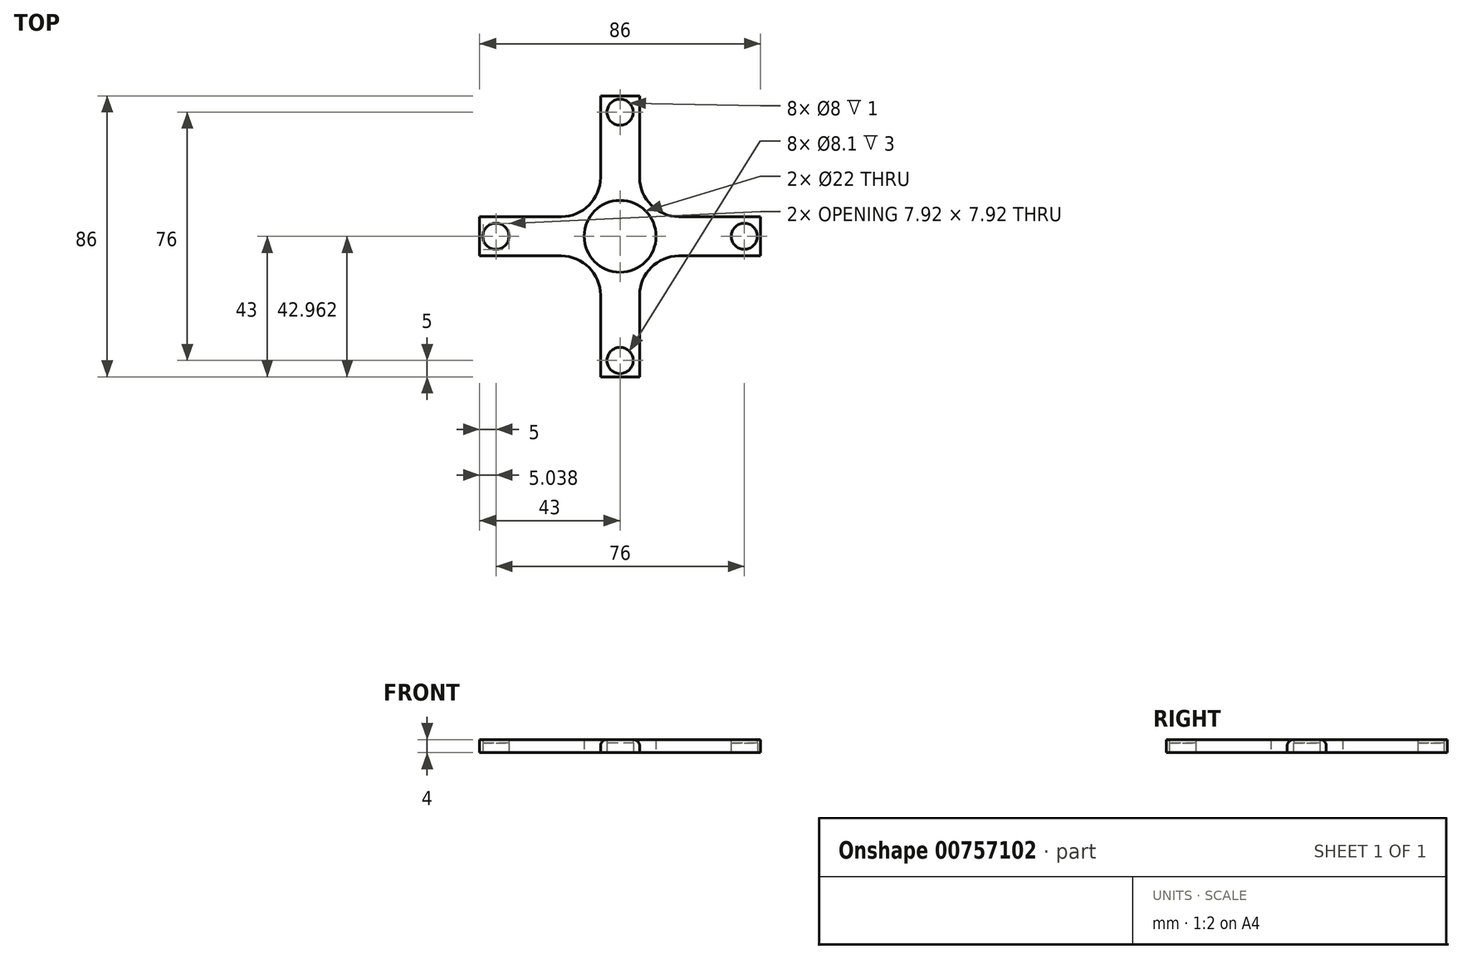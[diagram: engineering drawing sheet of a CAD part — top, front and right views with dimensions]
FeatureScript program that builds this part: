
annotation { "Feature Type Name" : "Feature", "Feature Type Description" : "" }
export const myFeature = defineFeature(function(context is Context, id is Id, definition is map)
    precondition{}
    {
        {
            var Q0;
            Q0=qCreatedBy(makeId("Top.planeOp"),FACE);
            var sketch = newSketch(context, id + "F0", { "sketchPlane" : qUnion([Q0])});
            skLineSegment(sketch, "E0.bottom", {"start": v(0, 0) * mm, "end": v(6, 0) * mm});
            skLineSegment(sketch, "E0.top", {"start": v(0, 38) * mm, "end": v(6, 38) * mm});
            skLineSegment(sketch, "E0.left", {"start": v(0, 0) * mm, "end": v(0, 38) * mm});
            skLineSegment(sketch, "E0.right", {"start": v(6, 18) * mm, "end": v(6, 38) * mm});
            skLineSegment(sketch, "E1.MirrorCS", {"start": v(0, 38) * mm, "end": v(-6, 38) * mm});
            skLineSegment(sketch, "E2.MirrorCS", {"start": v(-6, 18) * mm, "end": v(-6, 38) * mm});
            skLineSegment(sketch, "E3.MirrorCS", {"start": v(0, 0) * mm, "end": v(-6, 0) * mm});
            skLineSegment(sketch, "E4.1.0", {"start": v(-38, 0) * mm, "end": v(-38, -6) * mm});
            skLineSegment(sketch, "E4.1.1", {"start": v(-38, 0) * mm, "end": v(-38, 6) * mm});
            skLineSegment(sketch, "E4.1.2", {"start": v(-18, 6) * mm, "end": v(-38, 6) * mm});
            skLineSegment(sketch, "E4.1.3", {"start": v(-18, -6) * mm, "end": v(-38, -6) * mm});
            skLineSegment(sketch, "E4.1.4", {"start": v(0, 0) * mm, "end": v(0, -6) * mm});
            skLineSegment(sketch, "E4.1.5", {"start": v(0, 0) * mm, "end": v(0, 6) * mm});
            skLineSegment(sketch, "E4.2.0", {"start": v(0, -38) * mm, "end": v(6, -38) * mm});
            skLineSegment(sketch, "E4.2.1", {"start": v(0, -38) * mm, "end": v(-6, -38) * mm});
            skLineSegment(sketch, "E4.2.2", {"start": v(-6, -18) * mm, "end": v(-6, -38) * mm});
            skLineSegment(sketch, "E4.2.3", {"start": v(6, -18) * mm, "end": v(6, -38) * mm});
            skLineSegment(sketch, "E4.3.0", {"start": v(38, 0) * mm, "end": v(38, 6) * mm});
            skLineSegment(sketch, "E4.3.1", {"start": v(38, 0) * mm, "end": v(38, -6) * mm});
            skLineSegment(sketch, "E4.3.2", {"start": v(18, -6) * mm, "end": v(38, -6) * mm});
            skLineSegment(sketch, "E4.3.3", {"start": v(18, 6) * mm, "end": v(38, 6) * mm});
            skLineSegment(sketch, "E4.3.4", {"start": v(0, 0) * mm, "end": v(0, 6) * mm});
            skLineSegment(sketch, "E4.3.5", {"start": v(0, 0) * mm, "end": v(0, -6) * mm});
            skPoint(sketch, "E4.center", {"position": v(0, 0) * mm});
            skPoint(sketch, "E5.newPointA", {"position": v(-6, 0) * mm});
            skPoint(sketch, "E5.newPointB", {"position": v(0, 6) * mm});
            skArc(sketch, "E5.filletArc", {"start": v(-18, 6) * mm, "mid": v(-9.51, 9.51) * mm, "end": v(-6, 18) * mm});
            skPoint(sketch, "E6.newPointB", {"position": v(6, 0) * mm});
            skArc(sketch, "E6.filletArc", {"start": v(6, 18) * mm, "mid": v(9.51, 9.51) * mm, "end": v(18, 6) * mm});
            skPoint(sketch, "E7.newPointB", {"position": v(0, -6) * mm});
            skArc(sketch, "E7.filletArc", {"start": v(18, -6) * mm, "mid": v(9.51, -9.51) * mm, "end": v(6, -18) * mm});
            skArc(sketch, "E8.filletArc", {"start": v(-6, -18) * mm, "mid": v(-9.51, -9.51) * mm, "end": v(-18, -6) * mm});
            skCircle(sketch, "E9", {"center": v(38, 0) * mm, "radius": 4.05 * mm});
            skCircle(sketch, "E10", {"center": v(38, 0) * mm, "radius": 4 * mm});
            skLineSegment(sketch, "E11.bottom", {"start": v(38, 6) * mm, "end": v(43, 6) * mm});
            skLineSegment(sketch, "E11.top", {"start": v(38, -6) * mm, "end": v(43, -6) * mm});
            skLineSegment(sketch, "E11.left", {"start": v(38, 6) * mm, "end": v(38, -6) * mm});
            skLineSegment(sketch, "E11.right", {"start": v(43, 6) * mm, "end": v(43, -6) * mm});
            skLineSegment(sketch, "E12.1.0", {"start": v(-6, 38) * mm, "end": v(-6, 43) * mm});
            skLineSegment(sketch, "E12.1.1", {"start": v(-6, 43) * mm, "end": v(6, 43) * mm});
            skLineSegment(sketch, "E12.1.2", {"start": v(6, 38) * mm, "end": v(6, 43) * mm});
            skCircle(sketch, "E12.1.3", {"center": v(0, 38) * mm, "radius": 4 * mm});
            skCircle(sketch, "E12.1.4", {"center": v(0, 38) * mm, "radius": 4.05 * mm});
            skLineSegment(sketch, "E12.2.0", {"start": v(-38, -6) * mm, "end": v(-43, -6) * mm});
            skLineSegment(sketch, "E12.2.1", {"start": v(-43, -6) * mm, "end": v(-43, 6) * mm});
            skLineSegment(sketch, "E12.2.2", {"start": v(-38, 6) * mm, "end": v(-43, 6) * mm});
            skCircle(sketch, "E12.2.3", {"center": v(-38, 0) * mm, "radius": 4 * mm});
            skCircle(sketch, "E12.2.4", {"center": v(-38, 0) * mm, "radius": 4.05 * mm});
            skLineSegment(sketch, "E12.3.0", {"start": v(6, -38) * mm, "end": v(6, -43) * mm});
            skLineSegment(sketch, "E12.3.1", {"start": v(6, -43) * mm, "end": v(-6, -43) * mm});
            skLineSegment(sketch, "E12.3.2", {"start": v(-6, -38) * mm, "end": v(-6, -43) * mm});
            skCircle(sketch, "E12.3.3", {"center": v(0, -38) * mm, "radius": 4 * mm});
            skCircle(sketch, "E12.3.4", {"center": v(0, -38) * mm, "radius": 4.05 * mm});
            skCircle(sketch, "E13", {"center": v(0, 0) * mm, "radius": 11 * mm});
            skSolve(sketch);
        }
        {
            var Q0;
            {var subQ0=sQuery(id+"F0.wireOp",EDGE,"E12.1.0");Q0=makeQuery(id+"F0.imprint","IMPRINT",FACE,{"disambiguationData":[TD([[makeQuery(id+"F0.imprint","IMPRINT",EDGE,{"derivedFrom":subQ0}),-1.0]])]});}
            var Q1;
            {var subQ31=sQuery(id+"F0.wireOp",EDGE,"E0.right");Q1=makeQuery(id+"F0.imprint","IMPRINT",FACE,{"disambiguationData":[TD([[makeQuery(id+"F0.imprint","IMPRINT",EDGE,{"derivedFrom":subQ31}),1.0]])]});}
            var Q2;
            {var subQ1=sQuery(id+"F0.wireOp",EDGE,"E11.bottom");Q2=makeQuery(id+"F0.imprint","IMPRINT",FACE,{"disambiguationData":[TD([[makeQuery(id+"F0.imprint","IMPRINT",EDGE,{"derivedFrom":subQ1}),-1.0]])]});}
            var Q3;
            {var subQ0=sQuery(id+"F0.wireOp",EDGE,"E12.3.0");Q3=makeQuery(id+"F0.imprint","IMPRINT",FACE,{"disambiguationData":[TD([[makeQuery(id+"F0.imprint","IMPRINT",EDGE,{"derivedFrom":subQ0}),-1.0]])]});}
            var Q4;
            {var subQ6=sQuery(id+"F0.wireOp",EDGE,"E12.2.0");Q4=makeQuery(id+"F0.imprint","IMPRINT",FACE,{"disambiguationData":[TD([[makeQuery(id+"F0.imprint","IMPRINT",EDGE,{"derivedFrom":subQ6}),-1.0]])]});}
            var Q5;
            {var subQ0=sQuery(id+"F0.wireOp",EDGE,"E12.2.4");var subQ1=sQuery(id+"F0.wireOp",EDGE,"E4.1.0");var subQ2=makeQuery(id+"F0.imprint","INTERSECT",VERTEX,{"derivedFrom":[subQ1,subQ0]});Q5=makeQuery(id+"F0.imprint","IMPRINT",FACE,{"disambiguationData":[TD([[makeQuery(id+"F0.imprint","IMPRINT",EDGE,{"disambiguationData":[TD([[subQ2,-1.0]])],"derivedFrom":subQ1}),1.0]])]});}
            var Q6;
            {var subQ0=sQuery(id+"F0.wireOp",EDGE,"E12.2.4");var subQ1=sQuery(id+"F0.wireOp",EDGE,"E4.1.0");var subQ2=makeQuery(id+"F0.imprint","INTERSECT",VERTEX,{"derivedFrom":[subQ1,subQ0]});Q6=makeQuery(id+"F0.imprint","IMPRINT",FACE,{"disambiguationData":[TD([[makeQuery(id+"F0.imprint","IMPRINT",EDGE,{"disambiguationData":[TD([[subQ2,-1.0]])],"derivedFrom":subQ1}),-1.0]])]});}
            var Q7;
            {var subQ0=sQuery(id+"F0.wireOp",EDGE,"E11.left");var subQ1=sQuery(id+"F0.wireOp",EDGE,"E9");var subQ2=makeQuery(id+"F0.imprint","INTERSECT",VERTEX,{"disambiguationData":[OD(0.0)],"derivedFrom":[subQ1,subQ0]});Q7=makeQuery(id+"F0.imprint","IMPRINT",FACE,{"disambiguationData":[TD([[makeQuery(id+"F0.imprint","IMPRINT",EDGE,{"disambiguationData":[TD([[subQ2,-1.0]])],"derivedFrom":subQ1}),-1.0]])]});}
            var Q8;
            {var subQ0=sQuery(id+"F0.wireOp",EDGE,"E11.left");var subQ1=sQuery(id+"F0.wireOp",EDGE,"E9");var subQ2=makeQuery(id+"F0.imprint","INTERSECT",VERTEX,{"disambiguationData":[OD(0.0)],"derivedFrom":[subQ1,subQ0]});Q8=makeQuery(id+"F0.imprint","IMPRINT",FACE,{"disambiguationData":[TD([[makeQuery(id+"F0.imprint","IMPRINT",EDGE,{"disambiguationData":[TD([[subQ2,-1.0]])],"derivedFrom":subQ1}),1.0]])]});}
            var Q9;
            {var subQ0=sQuery(id+"F0.wireOp",EDGE,"E11.left");var subQ1=sQuery(id+"F0.wireOp",EDGE,"E9");var subQ2=makeQuery(id+"F0.imprint","INTERSECT",VERTEX,{"disambiguationData":[OD(0.0)],"derivedFrom":[subQ1,subQ0]});Q9=makeQuery(id+"F0.imprint","IMPRINT",FACE,{"disambiguationData":[TD([[makeQuery(id+"F0.imprint","IMPRINT",EDGE,{"disambiguationData":[TD([[subQ2,1.0]])],"derivedFrom":subQ1}),1.0]])]});}
            var Q10;
            {var subQ0=sQuery(id+"F0.wireOp",EDGE,"E11.left");var subQ1=sQuery(id+"F0.wireOp",EDGE,"E9");var subQ2=makeQuery(id+"F0.imprint","INTERSECT",VERTEX,{"disambiguationData":[OD(0.0)],"derivedFrom":[subQ1,subQ0]});Q10=makeQuery(id+"F0.imprint","IMPRINT",FACE,{"disambiguationData":[TD([[makeQuery(id+"F0.imprint","IMPRINT",EDGE,{"disambiguationData":[TD([[subQ2,1.0]])],"derivedFrom":subQ1}),-1.0]])]});}
            var Q11;
            {var subQ0=sQuery(id+"F0.wireOp",EDGE,"E12.3.4");var subQ1=sQuery(id+"F0.wireOp",EDGE,"E4.2.0");var subQ2=makeQuery(id+"F0.imprint","INTERSECT",VERTEX,{"derivedFrom":[subQ1,subQ0]});Q11=makeQuery(id+"F0.imprint","IMPRINT",FACE,{"disambiguationData":[TD([[makeQuery(id+"F0.imprint","IMPRINT",EDGE,{"disambiguationData":[TD([[subQ2,-1.0]])],"derivedFrom":subQ1}),1.0]])]});}
            var Q12;
            {var subQ0=sQuery(id+"F0.wireOp",EDGE,"E12.3.4");var subQ1=sQuery(id+"F0.wireOp",EDGE,"E4.2.0");var subQ2=makeQuery(id+"F0.imprint","INTERSECT",VERTEX,{"derivedFrom":[subQ1,subQ0]});Q12=makeQuery(id+"F0.imprint","IMPRINT",FACE,{"disambiguationData":[TD([[makeQuery(id+"F0.imprint","IMPRINT",EDGE,{"disambiguationData":[TD([[subQ2,-1.0]])],"derivedFrom":subQ1}),-1.0]])]});}
            var Q13;
            {var subQ0=sQuery(id+"F0.wireOp",EDGE,"E12.1.5");var subQ1=sQuery(id+"F0.wireOp",EDGE,"E0.top");var subQ2=makeQuery(id+"F0.imprint","INTERSECT",VERTEX,{"derivedFrom":[subQ1,subQ0]});Q13=makeQuery(id+"F0.imprint","IMPRINT",FACE,{"disambiguationData":[TD([[makeQuery(id+"F0.imprint","IMPRINT",EDGE,{"disambiguationData":[TD([[subQ2,-1.0]])],"derivedFrom":subQ1}),1.0]])]});}
            var Q14;
            {var subQ0=sQuery(id+"F0.wireOp",EDGE,"E12.1.4");var subQ1=sQuery(id+"F0.wireOp",EDGE,"E0.top");var subQ2=makeQuery(id+"F0.imprint","INTERSECT",VERTEX,{"derivedFrom":[subQ1,subQ0]});Q14=makeQuery(id+"F0.imprint","IMPRINT",FACE,{"disambiguationData":[TD([[makeQuery(id+"F0.imprint","IMPRINT",EDGE,{"disambiguationData":[TD([[subQ2,-1.0]])],"derivedFrom":subQ1}),1.0]])]});}
            var Q15;
            {var subQ0=sQuery(id+"F0.wireOp",EDGE,"E12.1.4");var subQ1=sQuery(id+"F0.wireOp",EDGE,"E0.top");var subQ2=makeQuery(id+"F0.imprint","INTERSECT",VERTEX,{"derivedFrom":[subQ1,subQ0]});Q15=makeQuery(id+"F0.imprint","IMPRINT",FACE,{"disambiguationData":[TD([[makeQuery(id+"F0.imprint","IMPRINT",EDGE,{"disambiguationData":[TD([[subQ2,-1.0]])],"derivedFrom":subQ1}),-1.0]])]});}
            var Q16;
            {var subQ0=sQuery(id+"F0.wireOp",EDGE,"E12.1.5");var subQ1=sQuery(id+"F0.wireOp",EDGE,"E0.top");var subQ2=makeQuery(id+"F0.imprint","INTERSECT",VERTEX,{"derivedFrom":[subQ1,subQ0]});Q16=makeQuery(id+"F0.imprint","IMPRINT",FACE,{"disambiguationData":[TD([[makeQuery(id+"F0.imprint","IMPRINT",EDGE,{"disambiguationData":[TD([[subQ2,-1.0]])],"derivedFrom":subQ1}),-1.0]])]});}
            var Q17;
            {var subQ0=sQuery(id+"F0.wireOp",EDGE,"E12.1.4");var subQ1=sQuery(id+"F0.wireOp",EDGE,"E0.left");var subQ2=makeQuery(id+"F0.imprint","INTERSECT",VERTEX,{"derivedFrom":[subQ1,subQ0]});Q17=makeQuery(id+"F0.imprint","IMPRINT",FACE,{"disambiguationData":[TD([[makeQuery(id+"F0.imprint","IMPRINT",EDGE,{"disambiguationData":[TD([[subQ2,-1.0]])],"derivedFrom":subQ1}),1.0]])]});}
            var Q18;
            {var subQ0=sQuery(id+"F0.wireOp",EDGE,"E12.2.3");var subQ1=sQuery(id+"F0.wireOp",EDGE,"E4.1.0");var subQ2=makeQuery(id+"F0.imprint","INTERSECT",VERTEX,{"derivedFrom":[subQ1,subQ0]});Q18=makeQuery(id+"F0.imprint","IMPRINT",FACE,{"disambiguationData":[TD([[makeQuery(id+"F0.imprint","IMPRINT",EDGE,{"disambiguationData":[TD([[subQ2,-1.0]])],"derivedFrom":subQ1}),1.0]])]});}
            var Q19;
            {var subQ0=sQuery(id+"F0.wireOp",EDGE,"E12.2.3");var subQ1=sQuery(id+"F0.wireOp",EDGE,"E4.1.0");var subQ2=makeQuery(id+"F0.imprint","INTERSECT",VERTEX,{"derivedFrom":[subQ1,subQ0]});Q19=makeQuery(id+"F0.imprint","IMPRINT",FACE,{"disambiguationData":[TD([[makeQuery(id+"F0.imprint","IMPRINT",EDGE,{"disambiguationData":[TD([[subQ2,-1.0]])],"derivedFrom":subQ1}),-1.0]])]});}
            var Q20;
            {var subQ0=sQuery(id+"F0.wireOp",EDGE,"E12.1.3");var subQ1=sQuery(id+"F0.wireOp",EDGE,"E0.top");var subQ2=makeQuery(id+"F0.imprint","INTERSECT",VERTEX,{"derivedFrom":[subQ1,subQ0]});Q20=makeQuery(id+"F0.imprint","IMPRINT",FACE,{"disambiguationData":[TD([[makeQuery(id+"F0.imprint","IMPRINT",EDGE,{"disambiguationData":[TD([[subQ2,-1.0]])],"derivedFrom":subQ1}),1.0]])]});}
            var Q21;
            {var subQ0=sQuery(id+"F0.wireOp",EDGE,"E12.1.3");var subQ1=sQuery(id+"F0.wireOp",EDGE,"E0.top");var subQ2=makeQuery(id+"F0.imprint","INTERSECT",VERTEX,{"derivedFrom":[subQ1,subQ0]});Q21=makeQuery(id+"F0.imprint","IMPRINT",FACE,{"disambiguationData":[TD([[makeQuery(id+"F0.imprint","IMPRINT",EDGE,{"disambiguationData":[TD([[subQ2,-1.0]])],"derivedFrom":subQ1}),-1.0]])]});}
            var Q22;
            {var subQ0=sQuery(id+"F0.wireOp",EDGE,"E12.3.3");var subQ1=sQuery(id+"F0.wireOp",EDGE,"E4.2.0");var subQ2=makeQuery(id+"F0.imprint","INTERSECT",VERTEX,{"derivedFrom":[subQ1,subQ0]});Q22=makeQuery(id+"F0.imprint","IMPRINT",FACE,{"disambiguationData":[TD([[makeQuery(id+"F0.imprint","IMPRINT",EDGE,{"disambiguationData":[TD([[subQ2,-1.0]])],"derivedFrom":subQ1}),1.0]])]});}
            var Q23;
            {var subQ0=sQuery(id+"F0.wireOp",EDGE,"E12.3.3");var subQ1=sQuery(id+"F0.wireOp",EDGE,"E4.2.0");var subQ2=makeQuery(id+"F0.imprint","INTERSECT",VERTEX,{"derivedFrom":[subQ1,subQ0]});Q23=makeQuery(id+"F0.imprint","IMPRINT",FACE,{"disambiguationData":[TD([[makeQuery(id+"F0.imprint","IMPRINT",EDGE,{"disambiguationData":[TD([[subQ2,-1.0]])],"derivedFrom":subQ1}),-1.0]])]});}
            extrude(context, id + "F1", {"entities" : qUnion([Q0, Q1, Q2, Q3, Q4, Q5, Q6, Q7, Q8, Q9, Q10, Q11, Q12, Q13, Q14, Q15, Q16, Q17, Q18, Q19, Q20, Q21, Q22, Q23]), "depth" : 4 * mm, "offsetDistance" : 25 * mm});
        }
        {
            var Q0;
            {var subQ0=sQuery(id+"F0.wireOp",EDGE,"E12.3.3");var subQ1=sQuery(id+"F0.wireOp",EDGE,"E4.2.0");var subQ2=makeQuery(id+"F0.imprint","INTERSECT",VERTEX,{"derivedFrom":[subQ1,subQ0]});Q0=makeQuery(id+"F0.imprint","IMPRINT",FACE,{"disambiguationData":[TD([[makeQuery(id+"F0.imprint","IMPRINT",EDGE,{"disambiguationData":[TD([[subQ2,-1.0]])],"derivedFrom":subQ1}),-1.0]])]});}
            var Q1;
            {var subQ0=sQuery(id+"F0.wireOp",EDGE,"E12.3.5");var subQ1=sQuery(id+"F0.wireOp",EDGE,"E4.2.0");var subQ2=makeQuery(id+"F0.imprint","INTERSECT",VERTEX,{"derivedFrom":[subQ1,subQ0]});Q1=makeQuery(id+"F0.imprint","IMPRINT",FACE,{"disambiguationData":[TD([[makeQuery(id+"F0.imprint","IMPRINT",EDGE,{"disambiguationData":[TD([[subQ2,-1.0]])],"derivedFrom":subQ1}),-1.0]])]});}
            var Q2;
            {var subQ0=sQuery(id+"F0.wireOp",EDGE,"E12.3.3");var subQ1=sQuery(id+"F0.wireOp",EDGE,"E4.2.0");var subQ2=makeQuery(id+"F0.imprint","INTERSECT",VERTEX,{"derivedFrom":[subQ1,subQ0]});Q2=makeQuery(id+"F0.imprint","IMPRINT",FACE,{"disambiguationData":[TD([[makeQuery(id+"F0.imprint","IMPRINT",EDGE,{"disambiguationData":[TD([[subQ2,-1.0]])],"derivedFrom":subQ1}),1.0]])]});}
            var Q3;
            {var subQ0=sQuery(id+"F0.wireOp",EDGE,"E12.3.5");var subQ1=sQuery(id+"F0.wireOp",EDGE,"E4.2.0");var subQ2=makeQuery(id+"F0.imprint","INTERSECT",VERTEX,{"derivedFrom":[subQ1,subQ0]});Q3=makeQuery(id+"F0.imprint","IMPRINT",FACE,{"disambiguationData":[TD([[makeQuery(id+"F0.imprint","IMPRINT",EDGE,{"disambiguationData":[TD([[subQ2,-1.0]])],"derivedFrom":subQ1}),1.0]])]});}
            var Q4;
            {var subQ0=sQuery(id+"F0.wireOp",EDGE,"E11.left");var subQ1=sQuery(id+"F0.wireOp",EDGE,"E9");var subQ2=makeQuery(id+"F0.imprint","INTERSECT",VERTEX,{"disambiguationData":[OD(0.0)],"derivedFrom":[subQ1,subQ0]});Q4=makeQuery(id+"F0.imprint","IMPRINT",FACE,{"disambiguationData":[TD([[makeQuery(id+"F0.imprint","IMPRINT",EDGE,{"disambiguationData":[TD([[subQ2,1.0]])],"derivedFrom":subQ1}),1.0]])]});}
            var Q5;
            {var subQ0=sQuery(id+"F0.wireOp",EDGE,"E11.left");var subQ1=sQuery(id+"F0.wireOp",EDGE,"E10");var subQ2=makeQuery(id+"F0.imprint","INTERSECT",VERTEX,{"disambiguationData":[OD(0.0)],"derivedFrom":[subQ1,subQ0]});Q5=makeQuery(id+"F0.imprint","IMPRINT",FACE,{"disambiguationData":[TD([[makeQuery(id+"F0.imprint","IMPRINT",EDGE,{"disambiguationData":[TD([[subQ2,1.0]])],"derivedFrom":subQ1}),1.0]])]});}
            var Q6;
            {var subQ0=sQuery(id+"F0.wireOp",EDGE,"E11.left");var subQ1=sQuery(id+"F0.wireOp",EDGE,"E9");var subQ2=makeQuery(id+"F0.imprint","INTERSECT",VERTEX,{"disambiguationData":[OD(0.0)],"derivedFrom":[subQ1,subQ0]});Q6=makeQuery(id+"F0.imprint","IMPRINT",FACE,{"disambiguationData":[TD([[makeQuery(id+"F0.imprint","IMPRINT",EDGE,{"disambiguationData":[TD([[subQ2,-1.0]])],"derivedFrom":subQ1}),1.0]])]});}
            var Q7;
            {var subQ0=sQuery(id+"F0.wireOp",EDGE,"E11.left");var subQ1=sQuery(id+"F0.wireOp",EDGE,"E10");var subQ2=makeQuery(id+"F0.imprint","INTERSECT",VERTEX,{"disambiguationData":[OD(0.0)],"derivedFrom":[subQ1,subQ0]});Q7=makeQuery(id+"F0.imprint","IMPRINT",FACE,{"disambiguationData":[TD([[makeQuery(id+"F0.imprint","IMPRINT",EDGE,{"disambiguationData":[TD([[subQ2,-1.0]])],"derivedFrom":subQ1}),1.0]])]});}
            var Q8;
            {var subQ0=sQuery(id+"F0.wireOp",EDGE,"E12.1.5");var subQ1=sQuery(id+"F0.wireOp",EDGE,"E0.top");var subQ2=makeQuery(id+"F0.imprint","INTERSECT",VERTEX,{"derivedFrom":[subQ1,subQ0]});Q8=makeQuery(id+"F0.imprint","IMPRINT",FACE,{"disambiguationData":[TD([[makeQuery(id+"F0.imprint","IMPRINT",EDGE,{"disambiguationData":[TD([[subQ2,-1.0]])],"derivedFrom":subQ1}),1.0]])]});}
            var Q9;
            {var subQ0=sQuery(id+"F0.wireOp",EDGE,"E12.1.5");var subQ1=sQuery(id+"F0.wireOp",EDGE,"E0.top");var subQ2=makeQuery(id+"F0.imprint","INTERSECT",VERTEX,{"derivedFrom":[subQ1,subQ0]});Q9=makeQuery(id+"F0.imprint","IMPRINT",FACE,{"disambiguationData":[TD([[makeQuery(id+"F0.imprint","IMPRINT",EDGE,{"disambiguationData":[TD([[subQ2,-1.0]])],"derivedFrom":subQ1}),-1.0]])]});}
            var Q10;
            {var subQ0=sQuery(id+"F0.wireOp",EDGE,"E12.1.3");var subQ1=sQuery(id+"F0.wireOp",EDGE,"E0.top");var subQ2=makeQuery(id+"F0.imprint","INTERSECT",VERTEX,{"derivedFrom":[subQ1,subQ0]});Q10=makeQuery(id+"F0.imprint","IMPRINT",FACE,{"disambiguationData":[TD([[makeQuery(id+"F0.imprint","IMPRINT",EDGE,{"disambiguationData":[TD([[subQ2,-1.0]])],"derivedFrom":subQ1}),1.0]])]});}
            var Q11;
            {var subQ0=sQuery(id+"F0.wireOp",EDGE,"E12.1.3");var subQ1=sQuery(id+"F0.wireOp",EDGE,"E0.top");var subQ2=makeQuery(id+"F0.imprint","INTERSECT",VERTEX,{"derivedFrom":[subQ1,subQ0]});Q11=makeQuery(id+"F0.imprint","IMPRINT",FACE,{"disambiguationData":[TD([[makeQuery(id+"F0.imprint","IMPRINT",EDGE,{"disambiguationData":[TD([[subQ2,-1.0]])],"derivedFrom":subQ1}),-1.0]])]});}
            var Q12;
            {var subQ0=sQuery(id+"F0.wireOp",EDGE,"E12.1.4");var subQ1=sQuery(id+"F0.wireOp",EDGE,"E0.left");var subQ2=makeQuery(id+"F0.imprint","INTERSECT",VERTEX,{"derivedFrom":[subQ1,subQ0]});Q12=makeQuery(id+"F0.imprint","IMPRINT",FACE,{"disambiguationData":[TD([[makeQuery(id+"F0.imprint","IMPRINT",EDGE,{"disambiguationData":[TD([[subQ2,-1.0]])],"derivedFrom":subQ1}),1.0]])]});}
            var Q13;
            {var subQ0=sQuery(id+"F0.wireOp",EDGE,"E12.1.3");var subQ1=sQuery(id+"F0.wireOp",EDGE,"E0.left");var subQ2=makeQuery(id+"F0.imprint","INTERSECT",VERTEX,{"derivedFrom":[subQ1,subQ0]});Q13=makeQuery(id+"F0.imprint","IMPRINT",FACE,{"disambiguationData":[TD([[makeQuery(id+"F0.imprint","IMPRINT",EDGE,{"disambiguationData":[TD([[subQ2,-1.0]])],"derivedFrom":subQ1}),1.0]])]});}
            var Q14;
            {var subQ0=sQuery(id+"F0.wireOp",EDGE,"E12.2.5");var subQ1=sQuery(id+"F0.wireOp",EDGE,"E4.1.0");var subQ2=makeQuery(id+"F0.imprint","INTERSECT",VERTEX,{"derivedFrom":[subQ1,subQ0]});Q14=makeQuery(id+"F0.imprint","IMPRINT",FACE,{"disambiguationData":[TD([[makeQuery(id+"F0.imprint","IMPRINT",EDGE,{"disambiguationData":[TD([[subQ2,-1.0]])],"derivedFrom":subQ1}),-1.0]])]});}
            var Q15;
            {var subQ0=sQuery(id+"F0.wireOp",EDGE,"E12.2.3");var subQ1=sQuery(id+"F0.wireOp",EDGE,"E4.1.0");var subQ2=makeQuery(id+"F0.imprint","INTERSECT",VERTEX,{"derivedFrom":[subQ1,subQ0]});Q15=makeQuery(id+"F0.imprint","IMPRINT",FACE,{"disambiguationData":[TD([[makeQuery(id+"F0.imprint","IMPRINT",EDGE,{"disambiguationData":[TD([[subQ2,-1.0]])],"derivedFrom":subQ1}),-1.0]])]});}
            var Q16;
            {var subQ0=sQuery(id+"F0.wireOp",EDGE,"E12.2.3");var subQ1=sQuery(id+"F0.wireOp",EDGE,"E4.1.0");var subQ2=makeQuery(id+"F0.imprint","INTERSECT",VERTEX,{"derivedFrom":[subQ1,subQ0]});Q16=makeQuery(id+"F0.imprint","IMPRINT",FACE,{"disambiguationData":[TD([[makeQuery(id+"F0.imprint","IMPRINT",EDGE,{"disambiguationData":[TD([[subQ2,-1.0]])],"derivedFrom":subQ1}),1.0]])]});}
            var Q17;
            {var subQ0=sQuery(id+"F0.wireOp",EDGE,"E12.2.5");var subQ1=sQuery(id+"F0.wireOp",EDGE,"E4.1.0");var subQ2=makeQuery(id+"F0.imprint","INTERSECT",VERTEX,{"derivedFrom":[subQ1,subQ0]});Q17=makeQuery(id+"F0.imprint","IMPRINT",FACE,{"disambiguationData":[TD([[makeQuery(id+"F0.imprint","IMPRINT",EDGE,{"disambiguationData":[TD([[subQ2,-1.0]])],"derivedFrom":subQ1}),1.0]])]});}
            extrude(context, id + "F2", {"entities" : qUnion([Q0, Q1, Q2, Q3, Q4, Q5, Q6, Q7, Q8, Q9, Q10, Q11, Q12, Q13, Q14, Q15, Q16, Q17]), "operationType" : NewBodyOperationType.REMOVE, "depth" : 3 * mm, "offsetDistance" : 25 * mm});
        }
        {
            var Q0;
            Q0=makeQuery(id+"F1.opExtrude","CAP_EDGE",EDGE,{"disambiguationData":[OSD([sQuery(id+"F0.wireOp",EDGE,"E2.MirrorCS"),sQuery(id+"F0.wireOp",EDGE,"E12.1.0")])],"isStart":false});
            var Q1;
            Q1=makeQuery(id+"F1.opExtrude","CAP_EDGE",EDGE,{"disambiguationData":[OSD([sQuery(id+"F0.wireOp",EDGE,"E0.right"),sQuery(id+"F0.wireOp",EDGE,"E12.1.2")])],"isStart":false});
            var Q2;
            Q2=makeQuery(id+"F1.opExtrude","CAP_EDGE",EDGE,{"disambiguationData":[OSD([sQuery(id+"F0.wireOp",EDGE,"E4.3.2"),sQuery(id+"F0.wireOp",EDGE,"E11.top")])],"isStart":false});
            var Q3;
            Q3=makeQuery(id+"F1.opExtrude","CAP_EDGE",EDGE,{"disambiguationData":[OSD([sQuery(id+"F0.wireOp",EDGE,"E7.filletArc")])],"isStart":false});
            var Q4;
            Q4=makeQuery(id+"F1.opExtrude","CAP_EDGE",EDGE,{"disambiguationData":[OSD([sQuery(id+"F0.wireOp",EDGE,"E8.filletArc")])],"isStart":false});
            fillet(context, id + "F3", {"entities" : qUnion([Q0, Q1, Q2, Q3, Q4]), "radius" : 2 * mm, "tangentPropagation" : true, "allowEdgeOverflow" : false});
        }
    });
